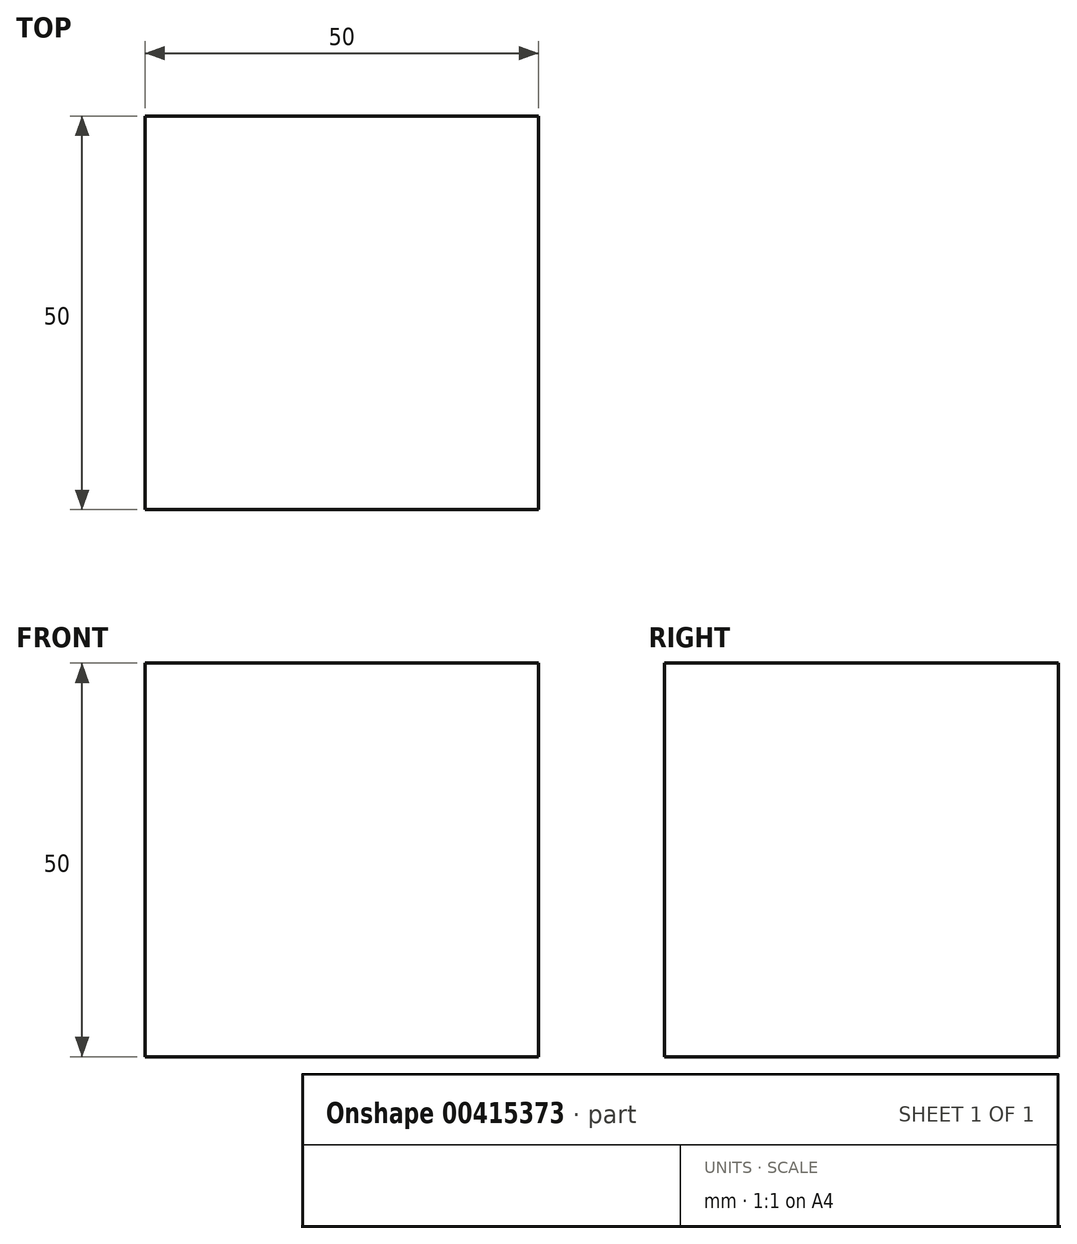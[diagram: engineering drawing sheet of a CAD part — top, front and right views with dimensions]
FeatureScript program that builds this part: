
annotation { "Feature Type Name" : "Feature", "Feature Type Description" : "" }
export const myFeature = defineFeature(function(context is Context, id is Id, definition is map)
    precondition{}
    {
        {
            var Q0;
            Q0=qCreatedBy(makeId("Top.planeOp"),FACE);
            var sketch = newSketch(context, id + "F0", { "sketchPlane" : qUnion([Q0])});
            skLineSegment(sketch, "E0.bottom", {"start": v(25, 25) * mm, "end": v(-25, 25) * mm});
            skLineSegment(sketch, "E0.top", {"start": v(25, -25) * mm, "end": v(-25, -25) * mm});
            skLineSegment(sketch, "E0.left", {"start": v(25, 25) * mm, "end": v(25, -25) * mm});
            skLineSegment(sketch, "E0.right", {"start": v(-25, 25) * mm, "end": v(-25, -25) * mm});
            skPoint(sketch, "E0.middle", {"position": v(0, 0) * mm});
            skSolve(sketch);
        }
        {
            var Q0;
            Q0=makeQuery(id+"F0.imprint","IMPRINT",FACE,{"disambiguationData":[TD([[makeQuery(id+"F0.imprint","IMPRINT",EDGE,{"derivedFrom":sQuery(id+"F0.wireOp",EDGE,"E0.bottom")}),1.0]])]});
            extrude(context, id + "F1", {"entities" : qUnion([Q0]), "depth" : 50 * mm, "offsetDistance" : 25 * mm});
        }
    });
